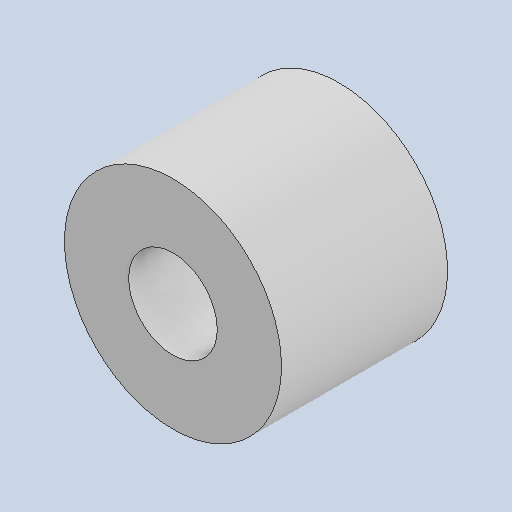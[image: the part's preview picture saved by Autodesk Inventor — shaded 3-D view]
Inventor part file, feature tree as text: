
AUTODESK INVENTOR PART (.ipt)
format: ipt  version: 2024 (Build 280153000, 153)  size: 98,816 bytes
history: native  units: in
note: dims shown in document units (in); Inventor stores cm internally (conversion verified against a paired STEP export)
features: extrude x1, sketch x1
ambient origin geometry x8: Origin, YZ Plane, XZ Plane, XY Plane, X Axis, Y Axis, Z Axis, Center Point
bodies: Solid1 (feature_tree)
feature tree (2):
  extrude  "Extrusion1"  Depth=0.375in
  sketch  "Sketch1"  dims[d0=0.2in d1=0.145in d2=0.375in d3=0.0in]
